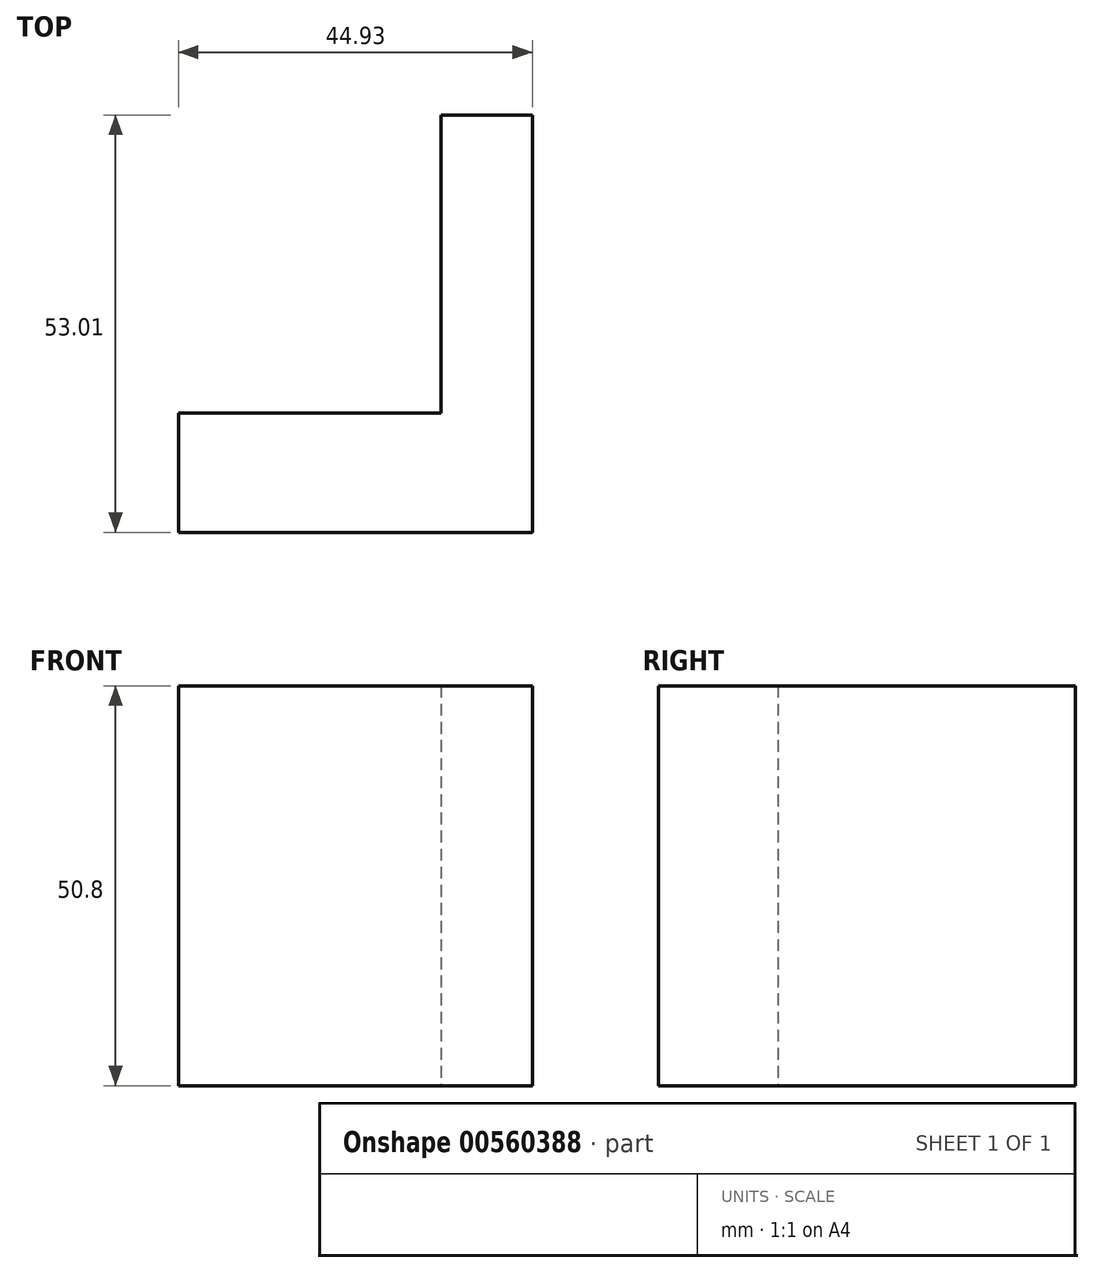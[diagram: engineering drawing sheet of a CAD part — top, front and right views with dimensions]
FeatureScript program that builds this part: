
annotation { "Feature Type Name" : "Feature", "Feature Type Description" : "" }
export const myFeature = defineFeature(function(context is Context, id is Id, definition is map)
    precondition{}
    {
        {
            var Q0;
            Q0=qCreatedBy(makeId("Top.planeOp"),FACE);
            var sketch = newSketch(context, id + "F0", { "sketchPlane" : qUnion([Q0])});
            skLineSegment(sketch, "E0.bottom", {"start": v(0, 15.17) * mm, "end": v(33.3, 15.17) * mm});
            skLineSegment(sketch, "E0.top", {"start": v(0, 0) * mm, "end": v(44.93, 0) * mm});
            skLineSegment(sketch, "E0.left", {"start": v(0, 15.17) * mm, "end": v(0, 0) * mm});
            skLineSegment(sketch, "E0.right", {"start": v(44.93, 15.17) * mm, "end": v(44.93, 0) * mm});
            skLineSegment(sketch, "E1.top", {"start": v(33.3, 53.01) * mm, "end": v(44.93, 53.01) * mm});
            skLineSegment(sketch, "E1.left", {"start": v(33.3, 15.17) * mm, "end": v(33.3, 53.01) * mm});
            skLineSegment(sketch, "E1.right", {"start": v(44.93, 15.17) * mm, "end": v(44.93, 53.01) * mm});
            skLineSegment(sketch, "E2.trimOffspring", {"start": v(44.93, 15.17) * mm, "end": v(44.93, 15.17) * mm});
            skSolve(sketch);
        }
        {
            var Q0;
            Q0=makeQuery(id+"F0.imprint","IMPRINT",FACE,{"disambiguationData":[TD([[makeQuery(id+"F0.imprint","IMPRINT",EDGE,{"derivedFrom":sQuery(id+"F0.wireOp",EDGE,"E0.bottom")}),-1.0]])]});
            extrude(context, id + "F1", {"entities" : qUnion([Q0]), "depth" : 50.8 * mm, "offsetDistance" : 25.4 * mm});
        }
    });
